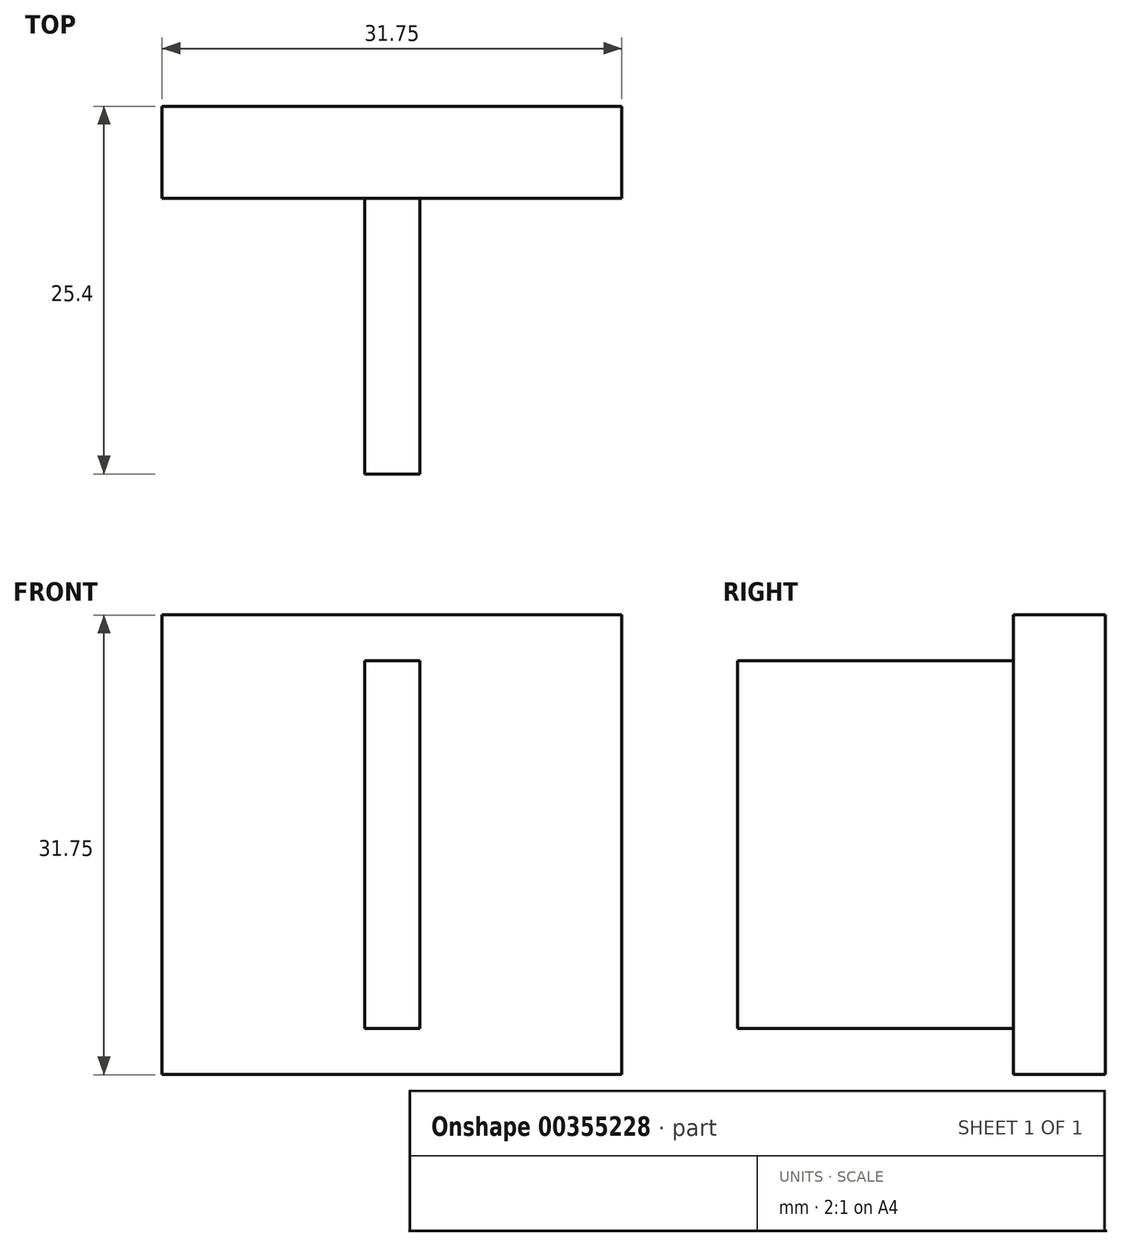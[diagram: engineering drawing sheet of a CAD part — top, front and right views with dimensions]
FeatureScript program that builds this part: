
annotation { "Feature Type Name" : "Feature", "Feature Type Description" : "" }
export const myFeature = defineFeature(function(context is Context, id is Id, definition is map)
    precondition{}
    {
        {
            var Q0;
            Q0=qCreatedBy(makeId("Top.planeOp"),FACE);
            var sketch = newSketch(context, id + "F0", { "sketchPlane" : qUnion([Q0])});
            skLineSegment(sketch, "E0.bottom", {"start": v(0, 0) * mm, "end": v(-3.8, 0) * mm});
            skLineSegment(sketch, "E0.top", {"start": v(0, 19.05) * mm, "end": v(-3.81, 19.05) * mm});
            skLineSegment(sketch, "E0.left", {"start": v(0, 0) * mm, "end": v(0, 19.05) * mm});
            skLineSegment(sketch, "E0.right", {"start": v(-3.8, 0) * mm, "end": v(-3.8, 19.05) * mm});
            skSolve(sketch);
        }
        {
            var Q0;
            Q0 = qSketchRegion(id + "F0", true);
            extrude(context, id + "F1", {"entities" : qUnion([Q0]), "depth" : 25.4 * mm, "offsetDistance" : 25.4 * mm});
        }
        {
            var Q0;
            Q0=makeQuery(id+"F1.opExtrude","SWEPT_FACE",FACE,{"disambiguationData":[OSD([sQuery(id+"F0.wireOp",EDGE,"E0.top")])]});
            var sketch = newSketch(context, id + "F2", { "sketchPlane" : qUnion([Q0])});
            skLineSegment(sketch, "E1.bottom", {"start": v(-13.96, 28.58) * mm, "end": v(17.79, 28.58) * mm});
            skLineSegment(sketch, "E1.top", {"start": v(-13.96, -3.17) * mm, "end": v(17.79, -3.17) * mm});
            skLineSegment(sketch, "E1.left", {"start": v(-13.96, 28.58) * mm, "end": v(-13.96, -3.17) * mm});
            skLineSegment(sketch, "E1.right", {"start": v(17.79, 28.58) * mm, "end": v(17.79, -3.17) * mm});
            skPoint(sketch, "E1.middle", {"position": v(1.91, 12.7) * mm});
            skPoint(sketch, "E1.middle.positionSnap0", {"position": v(0, 12.7) * mm});
            skPoint(sketch, "E1.centerSnap0", {"position": v(0, 12.7) * mm});
            skSolve(sketch);
        }
        {
            var Q0;
            Q0=makeQuery(id+"F2.imprint","IMPRINT",FACE,{"disambiguationData":[TD([[makeQuery(id+"F2.imprint","IMPRINT",EDGE,{"derivedFrom":sQuery(id+"F2.wireOp",EDGE,"E1.bottom")}),-1.0]])]});
            var Q1;
            {var subQ0=sQuery(id+"F0.wireOp",EDGE,"E0.top");Q1=makeQuery(id+"F2.imprint","IMPRINT",FACE,{"disambiguationData":[TD([[makeQuery(id+"F2.imprint","IMPRINT",EDGE,{"derivedFrom":makeQuery(id+"F1.opExtrude","CAP_EDGE",EDGE,{"disambiguationData":[OSD([subQ0])],"isStart":true})}),1.0]])]});}
            extrude(context, id + "F3", {"entities" : qUnion([Q0, Q1]), "operationType" : NewBodyOperationType.ADD, "depth" : 6.35 * mm, "offsetDistance" : 25.4 * mm});
        }
    });
